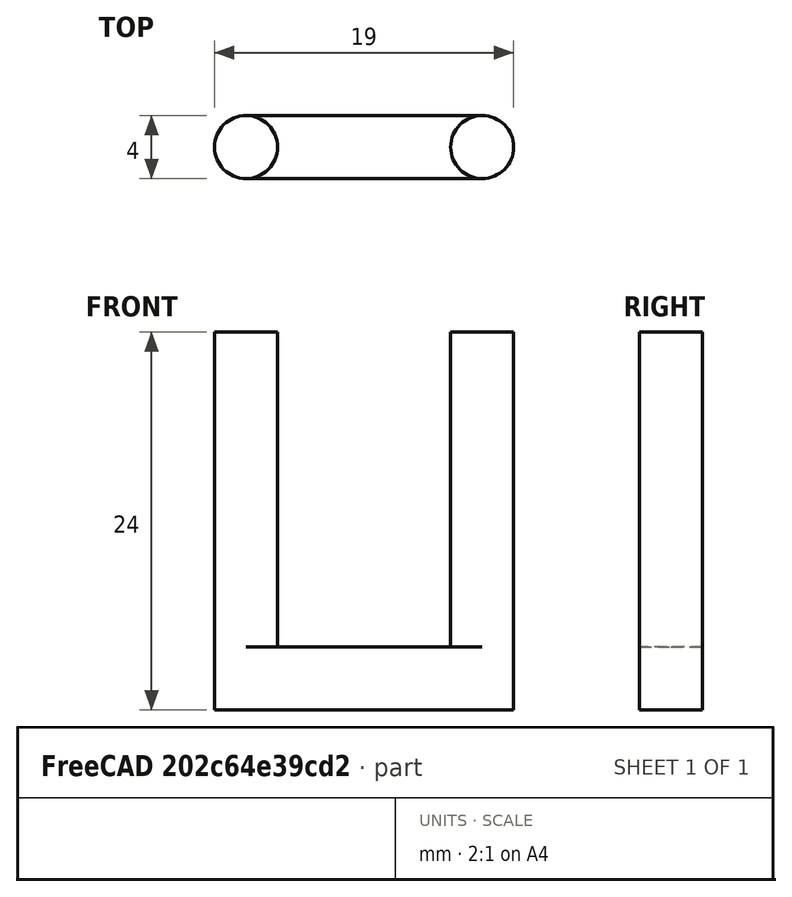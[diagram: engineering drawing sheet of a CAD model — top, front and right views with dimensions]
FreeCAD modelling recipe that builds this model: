
FCSTD DOCUMENT  (FreeCAD 0.20R29603 (Git))
Label: traba_puerta
License: All rights reserved
LicenseURL: http://en.wikipedia.org/wiki/All_rights_reserved
objects: Part::Cylinder×2, Sketcher::SketchObject×1, PartDesign::Pad×1, PartDesign::Body×1, Part::MultiFuse×1, Mesh::Feature×1
note: 7 computed .brp shape members not serialized (recipe doc carries the construction recipe); baked Part::Feature solids carry a one-line shape summary decoded from their .brp

FEATURE [Sketcher::SketchObject] Sketch
  FullyConstrained = true
  MapMode = 5
  Support = -> [XY_Plane]
  sketch-geometry (4):
    g0: ArcOfCircle CenterX=-7.5 CenterY=0 CenterZ=0 NormalX=0 NormalY=0 NormalZ=1 AngleXU=0 Radius=2 StartAngle=1.5708 EndAngle=4.71239
    g1: ArcOfCircle CenterX=7.5 CenterY=0 CenterZ=0 NormalX=0 NormalY=0 NormalZ=1 AngleXU=0 Radius=2 StartAngle=4.71239 EndAngle=7.85398
    g2: LineSegment StartX=-7.5 StartY=-2 StartZ=0 EndX=7.5 EndY=-2 EndZ=0
    g3: LineSegment StartX=7.5 StartY=2 StartZ=0 EndX=-7.5 EndY=2 EndZ=0
  constraints (9):
    c: Tangent(g0,g2) = -1.5708
    c: Tangent(g2,g1) = -1.5708
    c: Tangent(g1,g3) = -1.5708
    c: Tangent(g3,g0) = -1.5708
    c: Equal(g0,g1)
    c: PointOnObject(g0,g-1)
    c: DistanceX(g0,g1) = 15
    c: Symmetric(g0,g1,g-1)
    c: Radius(g1) = 2
FEATURE [PartDesign::Pad] Pad
  Direction = (0,0,1)
  Length = 4
  Length2 = 10
  Profile = -> Sketch
  ReferenceAxis = -> Sketch [N_Axis]
  Type = 0
FEATURE [PartDesign::Body] Body
  Group = -> [Sketch,Pad]
  Origin = -> Origin
  Tip = -> Pad
FEATURE [Part::Cylinder] Cylinder
  Angle = 360
  AttacherType = Attacher::AttachEngine3D
  FirstAngle = 0
  Height = 20
  Placement = pos=(-7.5,0,4) rot=(0,0,1;0rad)
  Radius = 2
  SecondAngle = 0
FEATURE [Part::Cylinder] Cylinder001
  Angle = 360
  AttacherType = Attacher::AttachEngine3D
  FirstAngle = 0
  Height = 20
  Placement = pos=(7.5,0,4) rot=(0,0,1;0rad)
  Radius = 2
  SecondAngle = 0
FEATURE [Part::MultiFuse] Fusion
  Shapes = -> [Body,Cylinder,Cylinder001]
FEATURE [Mesh::Feature] Mesh  label="Fusion (Meshed)"
